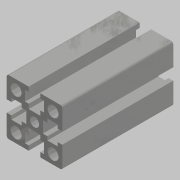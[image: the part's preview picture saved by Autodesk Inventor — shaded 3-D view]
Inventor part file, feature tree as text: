
AUTODESK INVENTOR PART (.ipt)
format: ipt  version: 2021.2 (Build 252289000, 289)  size: 211,456 bytes
history: native  units: in
note: dims shown in document units (in); Inventor stores cm internally (conversion verified against a paired STEP export)
features: other x2, extrude x1, sketch x1, projected_geometry x1
ambient origin geometry x8: Origin, YZ Plane, XZ Plane, XY Plane, X Axis, Y Axis, Z Axis, Center Point
bodies: Body1 (feature_tree)
feature tree (5):
  other  "ソリッド2"
  extrude  "押し出し1"  Depth=2.3622in
  sketch  "スケッチ2"
  projected_geometry  "投影ループ1"
  other  "ソリッド1"
